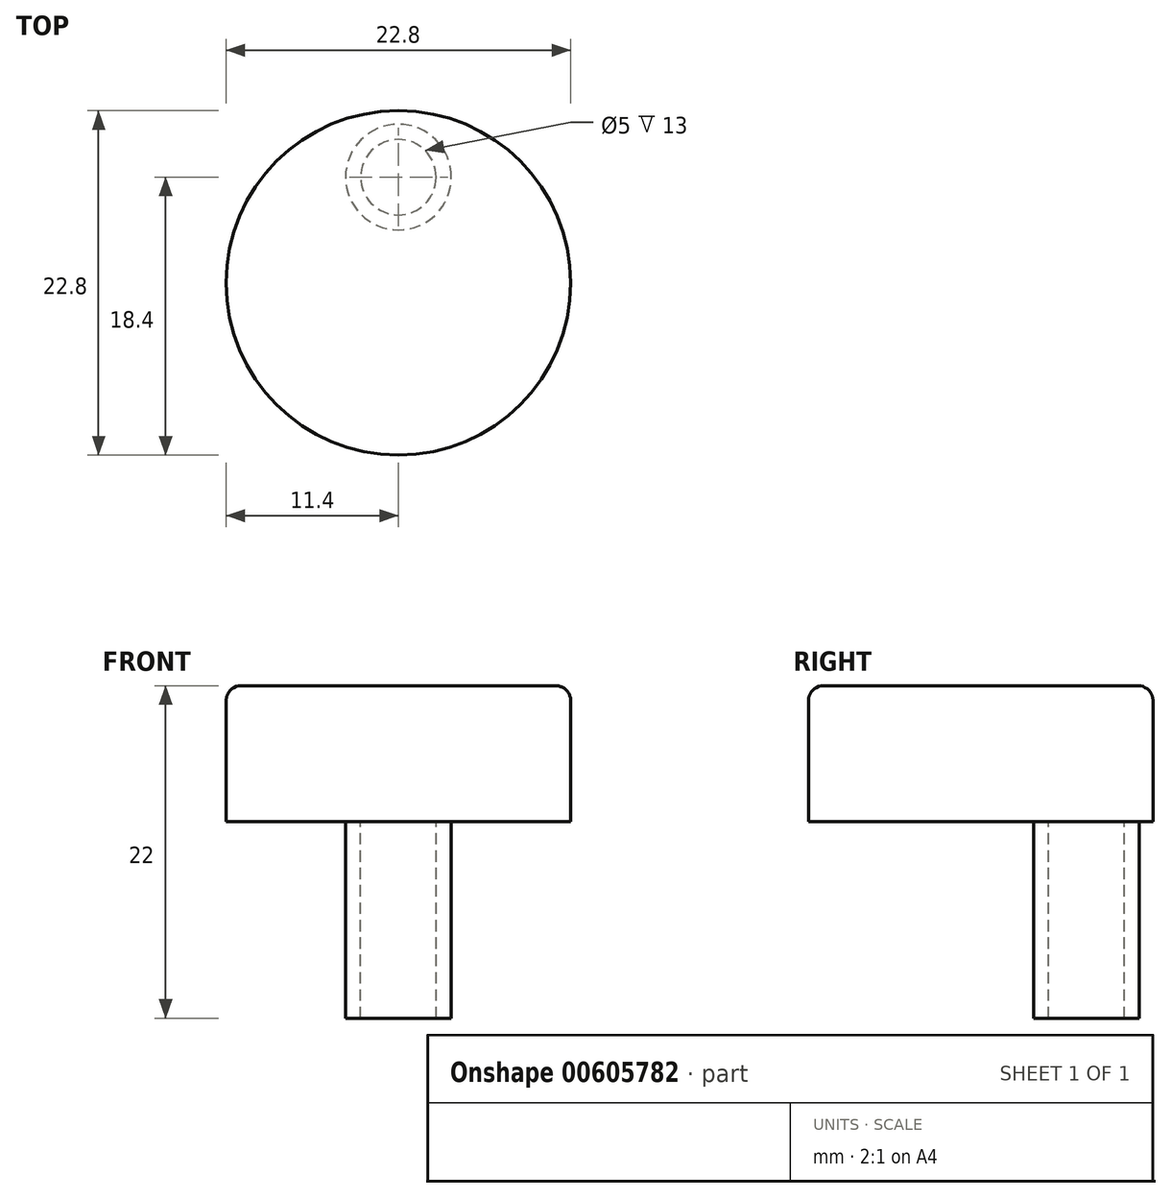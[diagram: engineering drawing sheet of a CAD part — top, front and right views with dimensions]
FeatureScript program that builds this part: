
annotation { "Feature Type Name" : "Feature", "Feature Type Description" : "" }
export const myFeature = defineFeature(function(context is Context, id is Id, definition is map)
    precondition{}
    {
        {
            var Q0;
            Q0=qCreatedBy(makeId("Top.planeOp"),FACE);
            var sketch = newSketch(context, id + "F0", { "sketchPlane" : qUnion([Q0])});
            skCircle(sketch, "E0", {"center": v(0, 0) * mm, "radius": 11.4 * mm});
            skSolve(sketch);
        }
        {
            var Q0;
            Q0=makeQuery(id+"F0.imprint","IMPRINT",FACE,{"disambiguationData":[TD([[makeQuery(id+"F0.imprint","IMPRINT",EDGE,{"derivedFrom":sQuery(id+"F0.wireOp",EDGE,"E0")}),1.0]])]});
            extrude(context, id + "F1", {"entities" : qUnion([Q0]), "depth" : 9 * mm, "offsetDistance" : 25 * mm});
        }
        {
            var Q0;
            Q0=makeQuery(id+"F1.opExtrude","CAP_FACE",FACE,{"disambiguationData":[OSD([sQuery(id+"F0.wireOp",EDGE,"E0")])],"isStart":true});
            var sketch = newSketch(context, id + "F2", { "sketchPlane" : qUnion([Q0])});
            skCircle(sketch, "E1", {"center": v(0, -7) * mm, "radius": 2.5 * mm});
            skCircle(sketch, "E2", {"center": v(0, -7) * mm, "radius": 3.5 * mm});
            skSolve(sketch);
        }
        {
            var Q0;
            Q0 = qSketchRegion(id + "F2", true);
            extrude(context, id + "F3", {"entities" : qUnion([Q0]), "operationType" : NewBodyOperationType.ADD, "depth" : 13 * mm, "offsetDistance" : 25 * mm});
        }
        {
            var Q0;
            Q0=makeQuery(id+"F1.opExtrude","CAP_EDGE",EDGE,{"disambiguationData":[OSD([sQuery(id+"F0.wireOp",EDGE,"E0")])],"isStart":false});
            fillet(context, id + "F4", {"entities" : qUnion([Q0]), "radius" : 1 * mm, "tangentPropagation" : true, "allowEdgeOverflow" : false});
        }
    });
